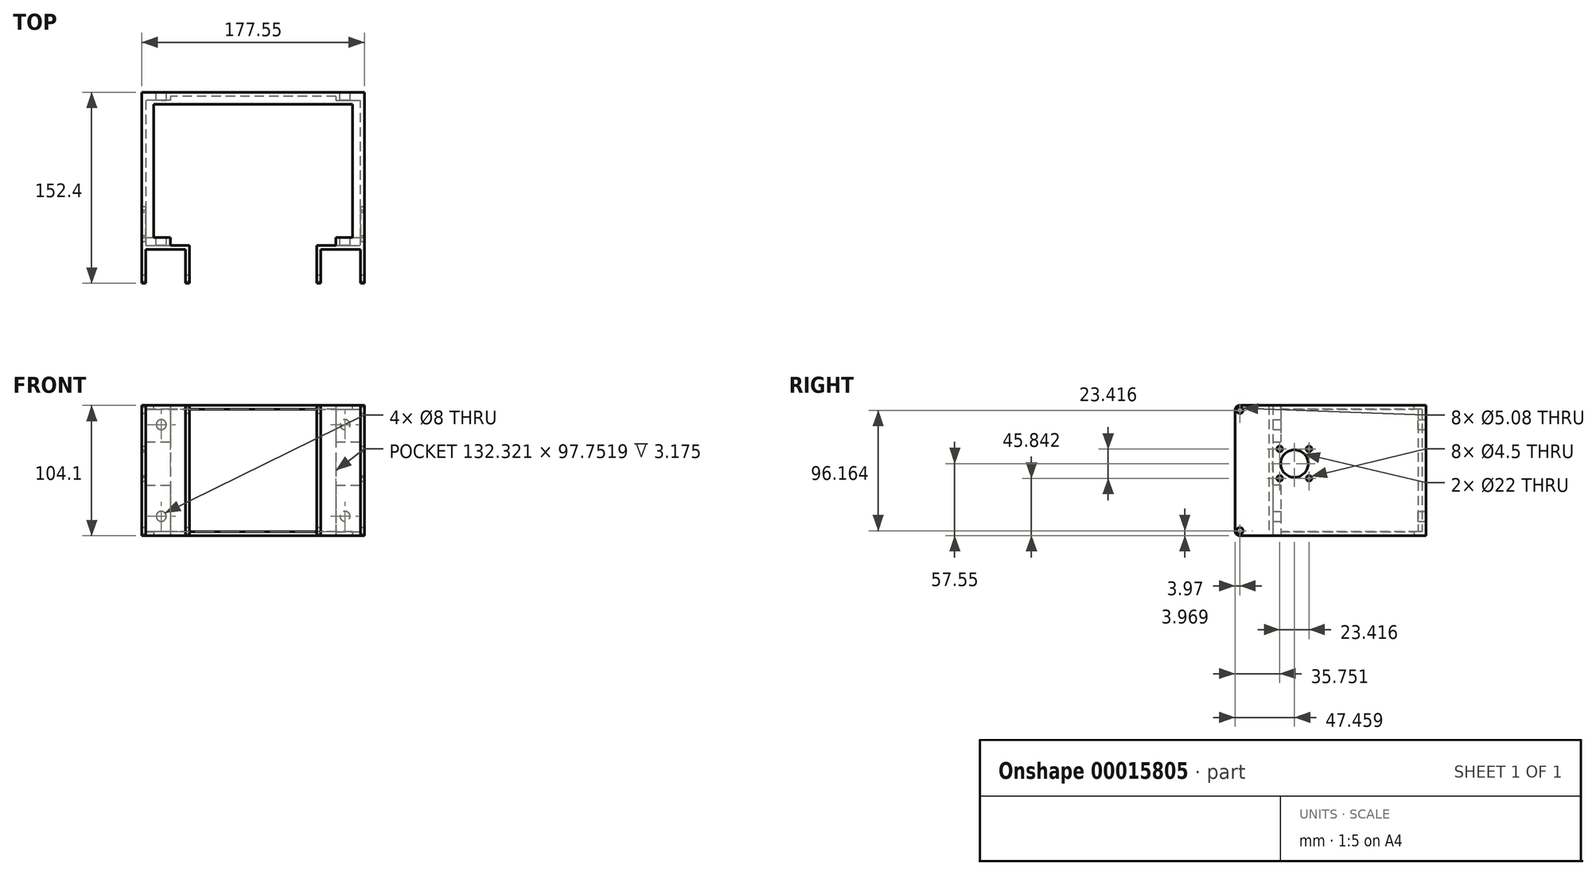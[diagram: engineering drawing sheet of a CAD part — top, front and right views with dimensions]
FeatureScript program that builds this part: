
annotation { "Feature Type Name" : "Feature", "Feature Type Description" : "" }
export const myFeature = defineFeature(function(context is Context, id is Id, definition is map)
    precondition{}
    {
        {
            var Q0;
            Q0=qCreatedBy(makeId("Top.planeOp"),FACE);
            var sketch = newSketch(context, id + "F0", { "sketchPlane" : qUnion([Q0])});
            skLineSegment(sketch, "E0.bottom", {"start": v(0, 0) * mm, "end": v(31.75, 0) * mm});
            skLineSegment(sketch, "E0.top", {"start": v(0, -27.02) * mm, "end": v(31.75, -27.02) * mm, "construction": true});
            skLineSegment(sketch, "E0.left", {"start": v(0, 0) * mm, "end": v(0, -27.02) * mm});
            skLineSegment(sketch, "E0.right", {"start": v(31.75, 0) * mm, "end": v(31.75, -27.02) * mm});
            skLineSegment(sketch, "E1", {"start": v(0, -27.02) * mm, "end": v(-3.18, -27.02) * mm});
            skLineSegment(sketch, "E2", {"start": v(-3.18, -27.02) * mm, "end": v(-3.18, 3.18) * mm});
            skLineSegment(sketch, "E3", {"start": v(-3.18, 3.17) * mm, "end": v(12.31, 3.17) * mm});
            skLineSegment(sketch, "E4", {"start": v(12.31, 3.18) * mm, "end": v(12.31, 9.53) * mm});
            skLineSegment(sketch, "E5", {"start": v(31.75, -27.02) * mm, "end": v(34.92, -27.02) * mm});
            skLineSegment(sketch, "E6", {"start": v(34.92, -27.02) * mm, "end": v(34.92, 125.38) * mm});
            skLineSegment(sketch, "E7", {"start": v(12.31, 3.18) * mm, "end": v(12.31, 0) * mm, "construction": true});
            skLineSegment(sketch, "E8", {"start": v(12.31, 9.52) * mm, "end": v(31.75, 9.52) * mm});
            skLineSegment(sketch, "E9", {"start": v(31.75, 9.53) * mm, "end": v(31.75, 119.03) * mm});
            skLineSegment(sketch, "E10", {"start": v(34.92, 125.38) * mm, "end": v(-142.62, 125.38) * mm});
            skLineSegment(sketch, "E11", {"start": v(12.31, 122.2) * mm, "end": v(-120, 122.2) * mm});
            skLineSegment(sketch, "E12", {"start": v(31.75, 64.28) * mm, "end": v(34.93, 64.28) * mm, "construction": true});
            skLineSegment(sketch, "E13", {"start": v(-53.85, 125.38) * mm, "end": v(-53.85, 122.2) * mm, "construction": true});
            skLineSegment(sketch, "E14.top", {"start": v(12.31, 119.03) * mm, "end": v(31.75, 119.03) * mm});
            skLineSegment(sketch, "E14.left", {"start": v(12.31, 122.2) * mm, "end": v(12.31, 119.03) * mm});
            skLineSegment(sketch, "E15", {"start": v(-120, 122.2) * mm, "end": v(-120, 119.03) * mm});
            skLineSegment(sketch, "E16", {"start": v(-120, 119.03) * mm, "end": v(-139.45, 119.03) * mm});
            skLineSegment(sketch, "E17", {"start": v(-139.45, 119.03) * mm, "end": v(-139.45, 9.52) * mm});
            skLineSegment(sketch, "E18", {"start": v(-139.45, 9.52) * mm, "end": v(-120, 9.52) * mm});
            skLineSegment(sketch, "E19", {"start": v(-120, 9.52) * mm, "end": v(-120, 3.17) * mm});
            skLineSegment(sketch, "E20", {"start": v(-120, 3.17) * mm, "end": v(-104.52, 3.17) * mm});
            skLineSegment(sketch, "E21", {"start": v(-104.52, 3.17) * mm, "end": v(-104.52, -27.02) * mm});
            skLineSegment(sketch, "E22", {"start": v(-104.52, -27.02) * mm, "end": v(-107.7, -27.02) * mm});
            skLineSegment(sketch, "E23", {"start": v(-107.7, -27.02) * mm, "end": v(-107.7, 0) * mm});
            skLineSegment(sketch, "E24", {"start": v(-107.7, 0) * mm, "end": v(-139.45, 0) * mm});
            skLineSegment(sketch, "E25", {"start": v(-139.45, 0) * mm, "end": v(-139.45, -27.02) * mm});
            skLineSegment(sketch, "E26", {"start": v(-139.45, -27.02) * mm, "end": v(-142.62, -27.02) * mm});
            skLineSegment(sketch, "E27", {"start": v(-142.62, -27.02) * mm, "end": v(-142.62, 125.38) * mm});
            skSolve(sketch);
        }
        {
            var Q0;
            Q0 = qSketchRegion(id + "F0", true);
            extrude(context, id + "F1", {"entities" : qUnion([Q0]), "depth" : 104.1 * mm});
        }
        {
            var Q0;
            Q0=makeQuery(id+"F1.opExtrude","SWEPT_FACE",FACE,{"disambiguationData":[OSD([sQuery(id+"F0.wireOp",EDGE,"E10")])]});
            var sketch = newSketch(context, id + "F2", { "sketchPlane" : qUnion([Q0])});
            skLineSegment(sketch, "E28.bottom", {"start": v(120, 104.1) * mm, "end": v(127.18, 104.1) * mm, "construction": true});
            skLineSegment(sketch, "E28.top", {"start": v(120, 88.66) * mm, "end": v(127.18, 88.66) * mm, "construction": true});
            skLineSegment(sketch, "E28.left", {"start": v(120, 104.1) * mm, "end": v(120, 88.66) * mm, "construction": true});
            skLineSegment(sketch, "E28.right", {"start": v(127.18, 104.1) * mm, "end": v(127.18, 88.66) * mm, "construction": true});
            skLineSegment(sketch, "E29.bottom", {"start": v(-12.31, 104.1) * mm, "end": v(-19.49, 104.1) * mm, "construction": true});
            skLineSegment(sketch, "E29.top", {"start": v(-12.31, 88.66) * mm, "end": v(-19.49, 88.66) * mm, "construction": true});
            skLineSegment(sketch, "E29.left", {"start": v(-12.31, 104.1) * mm, "end": v(-12.31, 88.66) * mm, "construction": true});
            skLineSegment(sketch, "E29.right", {"start": v(-19.49, 104.1) * mm, "end": v(-19.49, 88.66) * mm, "construction": true});
            skLineSegment(sketch, "E30.bottom", {"start": v(120, 0) * mm, "end": v(127.18, 0) * mm, "construction": true});
            skLineSegment(sketch, "E30.top", {"start": v(120, 15.44) * mm, "end": v(127.18, 15.44) * mm, "construction": true});
            skLineSegment(sketch, "E30.left", {"start": v(120, 0) * mm, "end": v(120, 15.44) * mm, "construction": true});
            skLineSegment(sketch, "E30.right", {"start": v(127.18, 0) * mm, "end": v(127.18, 15.44) * mm, "construction": true});
            skLineSegment(sketch, "E31.bottom", {"start": v(-12.31, 0) * mm, "end": v(-19.49, 0) * mm, "construction": true});
            skLineSegment(sketch, "E31.top", {"start": v(-12.31, 15.44) * mm, "end": v(-19.49, 15.44) * mm, "construction": true});
            skLineSegment(sketch, "E31.left", {"start": v(-12.31, 0) * mm, "end": v(-12.31, 15.44) * mm, "construction": true});
            skLineSegment(sketch, "E31.right", {"start": v(-19.49, 0) * mm, "end": v(-19.49, 15.44) * mm, "construction": true});
            skCircle(sketch, "E32", {"center": v(127.18, 88.66) * mm, "radius": 4 * mm});
            skCircle(sketch, "E33", {"center": v(127.18, 15.44) * mm, "radius": 4 * mm});
            skCircle(sketch, "E34", {"center": v(-19.49, 88.66) * mm, "radius": 4 * mm});
            skCircle(sketch, "E35", {"center": v(-19.49, 15.44) * mm, "radius": 4 * mm});
            skSolve(sketch);
        }
        {
            var Q0;
            Q0 = qSketchRegion(id + "F2", true);
            var Q1;
            Q1=makeQuery(id+"F1.opExtrude","SWEPT_FACE",FACE,{"disambiguationData":[OSD([sQuery(id+"F0.wireOp",EDGE,"E20")])]});
            extrude(context, id + "F3", {"entities" : qUnion([Q0]), "operationType" : NewBodyOperationType.REMOVE, "endBound" : BoundingType.UP_TO_SURFACE, "oppositeDirection" : true, "endBoundEntityFace" : qUnion([Q1]), "depth" : 25.4 * mm});
        }
        {
            var Q0;
            Q0=makeQuery(id+"F1.opExtrude","CAP_FACE",FACE,{"disambiguationData":[OSD([sQuery(id+"F0.wireOp",EDGE,"E0.bottom"),sQuery(id+"F0.wireOp",EDGE,"E0.left"),sQuery(id+"F0.wireOp",EDGE,"E0.right"),sQuery(id+"F0.wireOp",EDGE,"E1"),sQuery(id+"F0.wireOp",EDGE,"E2"),sQuery(id+"F0.wireOp",EDGE,"E3"),sQuery(id+"F0.wireOp",EDGE,"E4"),sQuery(id+"F0.wireOp",EDGE,"E5"),sQuery(id+"F0.wireOp",EDGE,"E6"),sQuery(id+"F0.wireOp",EDGE,"E8"),sQuery(id+"F0.wireOp",EDGE,"E9"),sQuery(id+"F0.wireOp",EDGE,"E10"),sQuery(id+"F0.wireOp",EDGE,"E11"),sQuery(id+"F0.wireOp",EDGE,"E14.top"),sQuery(id+"F0.wireOp",EDGE,"E14.left"),sQuery(id+"F0.wireOp",EDGE,"E15"),sQuery(id+"F0.wireOp",EDGE,"E16"),sQuery(id+"F0.wireOp",EDGE,"E17"),sQuery(id+"F0.wireOp",EDGE,"E18"),sQuery(id+"F0.wireOp",EDGE,"E19"),sQuery(id+"F0.wireOp",EDGE,"E20"),sQuery(id+"F0.wireOp",EDGE,"E21"),sQuery(id+"F0.wireOp",EDGE,"E22"),sQuery(id+"F0.wireOp",EDGE,"E23"),sQuery(id+"F0.wireOp",EDGE,"E24"),sQuery(id+"F0.wireOp",EDGE,"E25"),sQuery(id+"F0.wireOp",EDGE,"E26"),sQuery(id+"F0.wireOp",EDGE,"E27")])],"isStart":false});
            var sketch = newSketch(context, id + "F4", { "sketchPlane" : qUnion([Q0])});
            skLineSegment(sketch, "E36.bottom", {"start": v(-139.45, 9.52) * mm, "end": v(-133.1, 9.52) * mm});
            skLineSegment(sketch, "E36.top", {"start": v(-139.45, 119.03) * mm, "end": v(-120, 119.03) * mm});
            skLineSegment(sketch, "E36.left", {"start": v(-139.45, 9.52) * mm, "end": v(-139.45, 119.03) * mm});
            skLineSegment(sketch, "E36.right", {"start": v(-133.1, 9.52) * mm, "end": v(-133.1, 115.86) * mm});
            skLineSegment(sketch, "E37.bottom", {"start": v(31.75, 9.52) * mm, "end": v(25.4, 9.52) * mm});
            skLineSegment(sketch, "E37.top", {"start": v(31.75, 119.03) * mm, "end": v(12.31, 119.03) * mm});
            skLineSegment(sketch, "E37.left", {"start": v(31.75, 9.53) * mm, "end": v(31.75, 119.03) * mm});
            skLineSegment(sketch, "E37.right", {"start": v(25.4, 9.52) * mm, "end": v(25.4, 115.86) * mm});
            skLineSegment(sketch, "E38", {"start": v(-120, 119.03) * mm, "end": v(-120, 122.2) * mm});
            skLineSegment(sketch, "E39", {"start": v(-120, 122.2) * mm, "end": v(12.31, 122.2) * mm});
            skLineSegment(sketch, "E40", {"start": v(12.31, 122.2) * mm, "end": v(12.31, 119.03) * mm});
            skLineSegment(sketch, "E41", {"start": v(-133.1, 115.86) * mm, "end": v(25.4, 115.86) * mm});
            skLineSegment(sketch, "E42", {"start": v(-53.85, 122.2) * mm, "end": v(-53.85, 115.86) * mm, "construction": true});
            skSolve(sketch);
        }
        {
            var Q0;
            Q0 = qSketchRegion(id + "F4", true);
            extrude(context, id + "F5", {"entities" : qUnion([Q0]), "operationType" : NewBodyOperationType.ADD, "oppositeDirection" : true, "depth" : 3.17 * mm});
        }
        {
            var Q0;
            Q0=makeQuery(id+"F1.opExtrude","CAP_FACE",FACE,{"disambiguationData":[OSD([sQuery(id+"F0.wireOp",EDGE,"E0.bottom"),sQuery(id+"F0.wireOp",EDGE,"E0.left"),sQuery(id+"F0.wireOp",EDGE,"E0.right"),sQuery(id+"F0.wireOp",EDGE,"E1"),sQuery(id+"F0.wireOp",EDGE,"E2"),sQuery(id+"F0.wireOp",EDGE,"E3"),sQuery(id+"F0.wireOp",EDGE,"E4"),sQuery(id+"F0.wireOp",EDGE,"E5"),sQuery(id+"F0.wireOp",EDGE,"E6"),sQuery(id+"F0.wireOp",EDGE,"E8"),sQuery(id+"F0.wireOp",EDGE,"E9"),sQuery(id+"F0.wireOp",EDGE,"E10"),sQuery(id+"F0.wireOp",EDGE,"E11"),sQuery(id+"F0.wireOp",EDGE,"E14.top"),sQuery(id+"F0.wireOp",EDGE,"E14.left"),sQuery(id+"F0.wireOp",EDGE,"E15"),sQuery(id+"F0.wireOp",EDGE,"E16"),sQuery(id+"F0.wireOp",EDGE,"E17"),sQuery(id+"F0.wireOp",EDGE,"E18"),sQuery(id+"F0.wireOp",EDGE,"E19"),sQuery(id+"F0.wireOp",EDGE,"E20"),sQuery(id+"F0.wireOp",EDGE,"E21"),sQuery(id+"F0.wireOp",EDGE,"E22"),sQuery(id+"F0.wireOp",EDGE,"E23"),sQuery(id+"F0.wireOp",EDGE,"E24"),sQuery(id+"F0.wireOp",EDGE,"E25"),sQuery(id+"F0.wireOp",EDGE,"E26"),sQuery(id+"F0.wireOp",EDGE,"E27")])],"isStart":true});
            var sketch = newSketch(context, id + "F6", { "sketchPlane" : qUnion([Q0])});
            skLineSegment(sketch, "E43.bottom", {"start": v(31.75, -9.53) * mm, "end": v(25.4, -9.53) * mm});
            skLineSegment(sketch, "E43.top", {"start": v(31.75, -119.03) * mm, "end": v(12.31, -119.03) * mm});
            skLineSegment(sketch, "E43.left", {"start": v(31.75, -9.53) * mm, "end": v(31.75, -119.03) * mm});
            skLineSegment(sketch, "E43.right", {"start": v(25.4, -9.52) * mm, "end": v(25.4, -115.86) * mm});
            skLineSegment(sketch, "E44.bottom", {"start": v(-139.45, -9.52) * mm, "end": v(-133.1, -9.52) * mm});
            skLineSegment(sketch, "E44.top", {"start": v(-139.45, -119.03) * mm, "end": v(-120, -119.03) * mm});
            skLineSegment(sketch, "E44.left", {"start": v(-139.45, -9.52) * mm, "end": v(-139.45, -119.03) * mm});
            skLineSegment(sketch, "E44.right", {"start": v(-133.1, -9.53) * mm, "end": v(-133.1, -115.86) * mm});
            skLineSegment(sketch, "E45.top", {"start": v(12.31, -122.2) * mm, "end": v(-120, -122.2) * mm});
            skLineSegment(sketch, "E45.left", {"start": v(12.31, -119.03) * mm, "end": v(12.31, -122.2) * mm});
            skLineSegment(sketch, "E45.right", {"start": v(-120, -119.03) * mm, "end": v(-120, -122.2) * mm});
            skLineSegment(sketch, "E46", {"start": v(-53.85, -122.2) * mm, "end": v(-53.85, -115.86) * mm, "construction": true});
            skLineSegment(sketch, "E47", {"start": v(25.4, -115.86) * mm, "end": v(-133.1, -115.86) * mm});
            skSolve(sketch);
        }
        {
            var Q0;
            Q0 = qSketchRegion(id + "F6", true);
            extrude(context, id + "F7", {"entities" : qUnion([Q0]), "operationType" : NewBodyOperationType.ADD, "oppositeDirection" : true, "depth" : 3.17 * mm});
        }
        {
            var Q0;
            Q0=makeQuery(id+"F1.opExtrude","CAP_EDGE",EDGE,{"disambiguationData":[OSD([sQuery(id+"F0.wireOp",EDGE,"E5")])],"isStart":false});
            var Q1;
            Q1=makeQuery(id+"F1.opExtrude","CAP_EDGE",EDGE,{"disambiguationData":[OSD([sQuery(id+"F0.wireOp",EDGE,"E5")])],"isStart":true});
            var Q2;
            Q2=makeQuery(id+"F1.opExtrude","CAP_EDGE",EDGE,{"disambiguationData":[OSD([sQuery(id+"F0.wireOp",EDGE,"E1")])],"isStart":true});
            var Q3;
            Q3=makeQuery(id+"F1.opExtrude","CAP_EDGE",EDGE,{"disambiguationData":[OSD([sQuery(id+"F0.wireOp",EDGE,"E22")])],"isStart":true});
            var Q4;
            Q4=makeQuery(id+"F1.opExtrude","CAP_EDGE",EDGE,{"disambiguationData":[OSD([sQuery(id+"F0.wireOp",EDGE,"E26")])],"isStart":true});
            var Q5;
            Q5=makeQuery(id+"F1.opExtrude","CAP_EDGE",EDGE,{"disambiguationData":[OSD([sQuery(id+"F0.wireOp",EDGE,"E1")])],"isStart":false});
            var Q6;
            Q6=makeQuery(id+"F1.opExtrude","CAP_EDGE",EDGE,{"disambiguationData":[OSD([sQuery(id+"F0.wireOp",EDGE,"E22")])],"isStart":false});
            var Q7;
            Q7=makeQuery(id+"F1.opExtrude","CAP_EDGE",EDGE,{"disambiguationData":[OSD([sQuery(id+"F0.wireOp",EDGE,"E26")])],"isStart":false});
            fillet(context, id + "F8", {"entities" : qUnion([Q0, Q1, Q2, Q3, Q4, Q5, Q6, Q7]), "radius" : 3.97 * mm, "tangentPropagation" : true, "allowEdgeOverflow" : false});
        }
        {
            var Q0;
            Q0=makeQuery(id+"F1.opExtrude","SWEPT_FACE",FACE,{"disambiguationData":[OSD([sQuery(id+"F0.wireOp",EDGE,"E27")])]});
            var sketch = newSketch(context, id + "F9", { "sketchPlane" : qUnion([Q0])});
            skCircle(sketch, "E48", {"center": v(23.05, 3.97) * mm, "radius": 2.54 * mm});
            skCircle(sketch, "E49", {"center": v(23.05, 100.13) * mm, "radius": 2.54 * mm});
            skSolve(sketch);
        }
        {
            var Q0;
            Q0 = qSketchRegion(id + "F9", true);
            var Q1;
            Q1=makeQuery(id+"F1.opExtrude","SWEPT_FACE",FACE,{"disambiguationData":[OSD([sQuery(id+"F0.wireOp",EDGE,"E6")])]});
            extrude(context, id + "F10", {"entities" : qUnion([Q0]), "operationType" : NewBodyOperationType.REMOVE, "endBound" : BoundingType.UP_TO_SURFACE, "oppositeDirection" : true, "endBoundEntityFace" : qUnion([Q1]), "depth" : 25.4 * mm});
        }
        {
            var Q0;
            Q0=makeQuery(id+"F1.opExtrude","SWEPT_FACE",FACE,{"disambiguationData":[OSD([sQuery(id+"F0.wireOp",EDGE,"E19")])]});
            var sketch = newSketch(context, id + "F11", { "sketchPlane" : qUnion([Q0])});
            skLineSegment(sketch, "E50", {"start": v(6.35, 104.1) * mm, "end": v(6.35, 74.81) * mm, "construction": true});
            skLineSegment(sketch, "E51.bottom", {"start": v(3.17, 74.81) * mm, "end": v(9.52, 74.81) * mm});
            skLineSegment(sketch, "E51.top", {"start": v(3.17, 40.29) * mm, "end": v(9.52, 40.29) * mm});
            skLineSegment(sketch, "E51.left", {"start": v(3.17, 74.81) * mm, "end": v(3.17, 40.29) * mm});
            skLineSegment(sketch, "E51.right", {"start": v(9.52, 74.81) * mm, "end": v(9.52, 40.29) * mm});
            skPoint(sketch, "E52", {"position": v(9.52, 88.66) * mm});
            skSolve(sketch);
        }
        {
            var Q0;
            Q0 = qSketchRegion(id + "F11", true);
            var Q1;
            Q1=makeQuery(id+"F1.opExtrude","SWEPT_FACE",FACE,{"disambiguationData":[OSD([sQuery(id+"F0.wireOp",EDGE,"E17")])]});
            var Q2;
            Q2=makeQuery(id+"F1.opExtrude","SWEPT_FACE",FACE,{"disambiguationData":[OSD([sQuery(id+"F0.wireOp",EDGE,"E9")])]});
            extrude(context, id + "F12", {"entities" : qUnion([Q0]), "operationType" : NewBodyOperationType.REMOVE, "endBound" : BoundingType.UP_TO_SURFACE, "oppositeDirection" : true, "endBoundEntityFace" : qUnion([Q1]), "depth" : 25.4 * mm, "hasSecondDirection" : true, "secondDirectionBound" : BoundingType.UP_TO_SURFACE, "secondDirectionOppositeDirection" : false, "secondDirectionBoundEntityFace" : qUnion([Q2]), "secondDirectionDepth" : 25.4 * mm});
        }
        {
            var Q0;
            {var subQ0=sQuery(id+"F0.wireOp",EDGE,"E17");Q0=makeQuery(id+"F12.boolean.opBoolean","MERGE",FACE,{"derivedFrom":[makeQuery(id+"F1.opExtrude","SWEPT_FACE",FACE,{"disambiguationData":[OSD([subQ0])]}),makeQuery(id+"F12.opExtrude","CAP_FACE",FACE,{"disambiguationData":[OSD([subQ0])],"isStart":false})]});}
            var sketch = newSketch(context, id + "F13", { "sketchPlane" : qUnion([Q0])});
            skLineSegment(sketch, "E53", {"start": v(3.17, 57.55) * mm, "end": v(8.73, 57.55) * mm, "construction": true});
            skLineSegment(sketch, "E54.rect.bottom", {"start": v(32.15, 45.84) * mm, "end": v(8.73, 45.84) * mm, "construction": true});
            skLineSegment(sketch, "E54.rect.top", {"start": v(32.15, 69.26) * mm, "end": v(8.73, 69.26) * mm, "construction": true});
            skLineSegment(sketch, "E54.rect.left", {"start": v(32.15, 45.84) * mm, "end": v(32.15, 69.26) * mm, "construction": true});
            skLineSegment(sketch, "E54.rect.right", {"start": v(8.73, 45.84) * mm, "end": v(8.73, 69.26) * mm, "construction": true});
            skPoint(sketch, "E54.rect.middle", {"position": v(20.44, 57.55) * mm});
            skCircle(sketch, "E55", {"center": v(20.44, 57.55) * mm, "radius": 11 * mm});
            skCircle(sketch, "E56", {"center": v(32.15, 69.26) * mm, "radius": 2.25 * mm});
            skCircle(sketch, "E57", {"center": v(32.15, 45.84) * mm, "radius": 2.25 * mm});
            skCircle(sketch, "E58", {"center": v(8.73, 45.84) * mm, "radius": 2.25 * mm});
            skCircle(sketch, "E59", {"center": v(8.73, 69.26) * mm, "radius": 2.25 * mm});
            skSolve(sketch);
        }
        {
            var Q0;
            Q0 = qSketchRegion(id + "F13", true);
            var Q1;
            Q1=makeQuery(id+"F1.opExtrude","SWEPT_FACE",FACE,{"disambiguationData":[OSD([sQuery(id+"F0.wireOp",EDGE,"E27")])]});
            var Q2;
            Q2=makeQuery(id+"F1.opExtrude","SWEPT_FACE",FACE,{"disambiguationData":[OSD([sQuery(id+"F0.wireOp",EDGE,"E6")])]});
            extrude(context, id + "F14", {"entities" : qUnion([Q0]), "operationType" : NewBodyOperationType.REMOVE, "endBound" : BoundingType.UP_TO_SURFACE, "oppositeDirection" : true, "endBoundEntityFace" : qUnion([Q1]), "depth" : 25.4 * mm, "hasSecondDirection" : true, "secondDirectionBound" : BoundingType.UP_TO_SURFACE, "secondDirectionOppositeDirection" : false, "secondDirectionBoundEntityFace" : qUnion([Q2]), "secondDirectionDepth" : 25.4 * mm});
        }
    });
